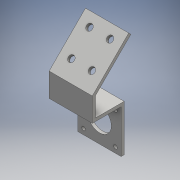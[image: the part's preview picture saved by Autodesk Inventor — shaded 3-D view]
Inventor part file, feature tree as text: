
AUTODESK INVENTOR PART (.ipt)
format: ipt  version: 2016 (Build 200138000, 138)  size: 173,056 bytes
history: native  units: mm
features: extrude x7, sketch x7, plane x1, projected_geometry x1
ambient origin geometry x8: Origin, YZ Plane, XZ Plane, XY Plane, X Axis, Y Axis, Z Axis, Center Point
bodies: Body1 (feature_tree)
feature tree (16):
  extrude  "拉伸2"  Depth=42.0mm
  extrude  "拉伸3"  Depth=3.0mm
  plane  "工作平面1"
  extrude  "拉伸6"  TaperAngle=45.0deg  [1 undecoded]
  extrude  "拉伸8"  Depth=3.5mm
  extrude  "拉伸9"  Depth=15.5mm
  extrude  "拉伸10"  Depth=15.5mm
  extrude  "拉伸11"  Depth=3.0mm
  sketch  "草图2"  dims[d3=42.0mm d4=42.0mm]
  sketch  "草图3"  dims[d5=3.0mm d6=0.0mm d7=51.0mm]
  sketch  "草图7"  dims[d8=3.0mm d9=0.0mm d10=45.0deg]
  sketch  "草图9"  dims[d17=23.0mm d18=3.5mm]
  sketch  "草图10"  dims[d19=15.5mm d20=15.5mm]
  projected_geometry  "投影回路1"
  sketch  "草图11"  dims[d21=15.5mm d22=15.5mm]
  sketch  "草图12"  dims[d23=3.0mm d24=0.0mm d32=3.0mm d33=20.0mm d34=20.0mm d35=0.0mm d36=20.0mm d37=0.0mm d38=42.0mm d39=50.0mm d40=3.0mm d41=0.0mm d42=6.0mm d43=10.0mm d44=15.0mm d45=25.0mm d46=3.0mm d47=0.0mm]
note: 1 required parameter value undecoded (feature->parameter linkage not recoverable at this tier; creation-order binding heuristic only, values carry confidence <= 0.55)
